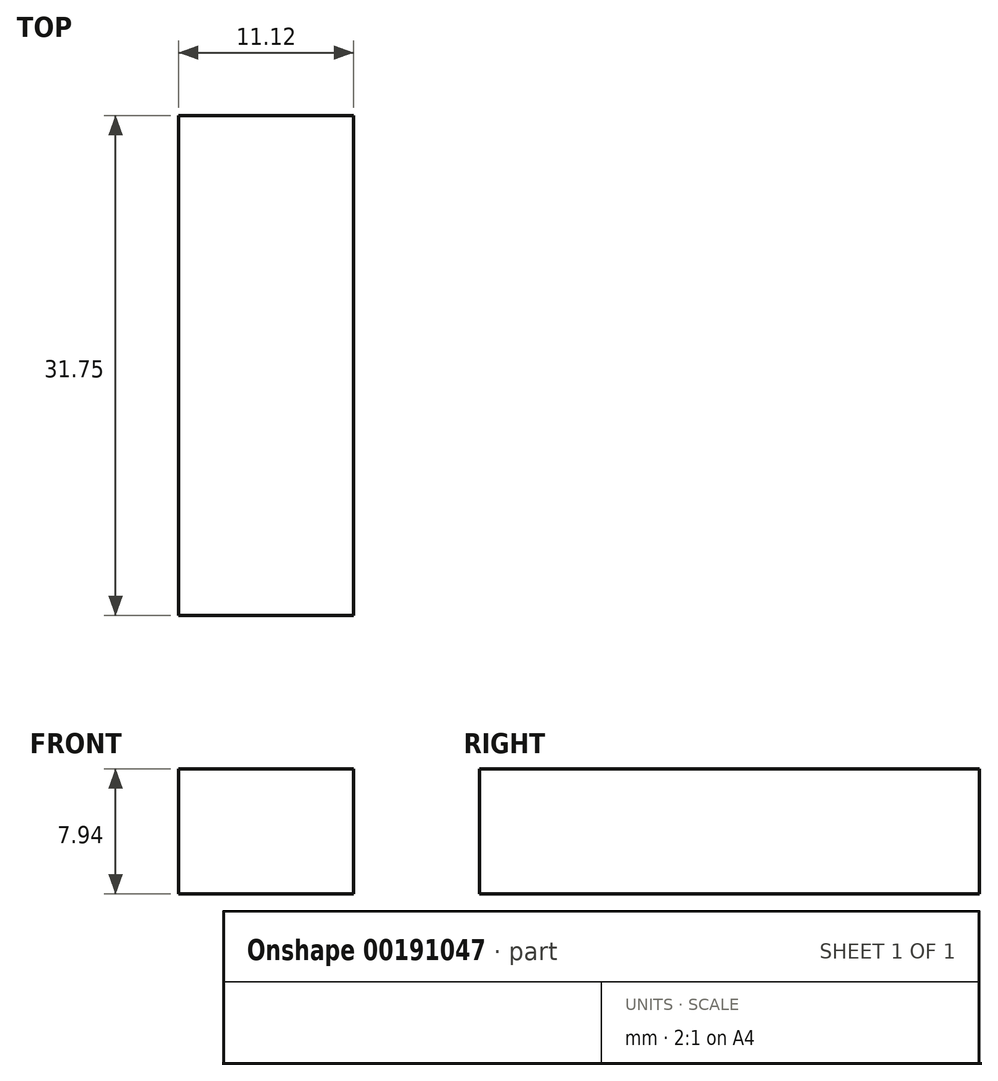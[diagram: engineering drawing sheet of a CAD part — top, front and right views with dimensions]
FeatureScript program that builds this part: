
annotation { "Feature Type Name" : "Feature", "Feature Type Description" : "" }
export const myFeature = defineFeature(function(context is Context, id is Id, definition is map)
    precondition{}
    {
        {
            var Q0;
            Q0=qCreatedBy(makeId("Front.planeOp"),FACE);
            var sketch = newSketch(context, id + "F0", { "sketchPlane" : qUnion([Q0])});
            skLineSegment(sketch, "E0.bottom", {"start": v(5.56, 3.97) * mm, "end": v(-5.56, 3.97) * mm});
            skLineSegment(sketch, "E0.top", {"start": v(5.56, -3.97) * mm, "end": v(-5.56, -3.97) * mm});
            skLineSegment(sketch, "E0.left", {"start": v(5.56, 3.97) * mm, "end": v(5.56, -3.97) * mm});
            skLineSegment(sketch, "E0.right", {"start": v(-5.56, 3.97) * mm, "end": v(-5.56, -3.97) * mm});
            skPoint(sketch, "E0.middle", {"position": v(0, 0) * mm});
            skSolve(sketch);
        }
        {
            var Q0;
            Q0=makeQuery(id+"F0.imprint","IMPRINT",FACE,{"disambiguationData":[TD([[makeQuery(id+"F0.imprint","IMPRINT",EDGE,{"derivedFrom":sQuery(id+"F0.wireOp",EDGE,"E0.bottom")}),1.0]])]});
            extrude(context, id + "F1", {"entities" : qUnion([Q0]), "depth" : 31.75 * mm});
        }
    });
